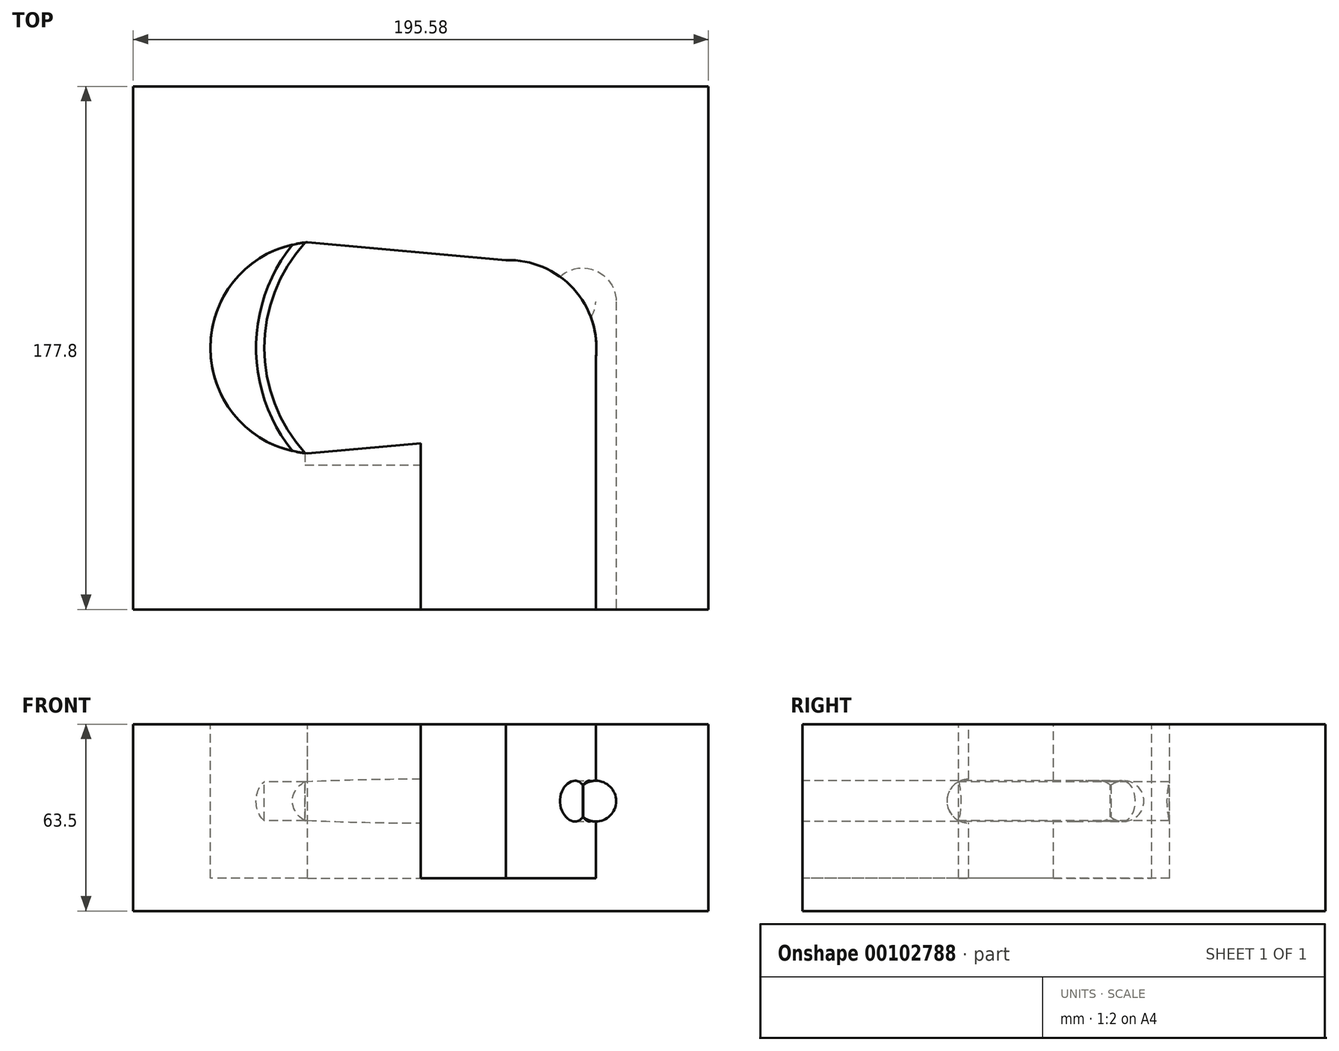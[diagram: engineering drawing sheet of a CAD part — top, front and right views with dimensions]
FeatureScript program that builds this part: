
annotation { "Feature Type Name" : "Feature", "Feature Type Description" : "" }
export const myFeature = defineFeature(function(context is Context, id is Id, definition is map)
    precondition{}
    {
        {
            var Q0;
            Q0=qCreatedBy(makeId("Top.planeOp"),FACE);
            var sketch = newSketch(context, id + "F0", { "sketchPlane" : qUnion([Q0])});
            skLineSegment(sketch, "E0.bottom", {"start": v(97.8, -88.9) * mm, "end": v(-97.8, -88.9) * mm});
            skLineSegment(sketch, "E0.top", {"start": v(97.8, 88.9) * mm, "end": v(-97.8, 88.9) * mm});
            skLineSegment(sketch, "E0.left", {"start": v(97.8, -88.9) * mm, "end": v(97.8, 88.9) * mm});
            skLineSegment(sketch, "E0.right", {"start": v(-97.8, -88.9) * mm, "end": v(-97.8, 88.9) * mm});
            skPoint(sketch, "E0.middle", {"position": v(0, 0) * mm});
            skSolve(sketch);
        }
        {
            var Q0;
            Q0 = qSketchRegion(id + "F0", true);
            extrude(context, id + "F1", {"entities" : qUnion([Q0]), "depth" : 63.5 * mm});
        }
        {
            var Q0;
            Q0=makeQuery(id+"F1.opExtrude","CAP_FACE",FACE,{"disambiguationData":[OSD([sQuery(id+"F0.wireOp",EDGE,"E0.bottom"),sQuery(id+"F0.wireOp",EDGE,"E0.top"),sQuery(id+"F0.wireOp",EDGE,"E0.left"),sQuery(id+"F0.wireOp",EDGE,"E0.right")])],"isStart":false});
            var sketch = newSketch(context, id + "F2", { "sketchPlane" : qUnion([Q0])});
            skLineSegment(sketch, "E1.bottom", {"start": v(94.69, -84.95) * mm, "end": v(59.47, -84.95) * mm});
            skLineSegment(sketch, "E1.top", {"start": v(94.69, 84.95) * mm, "end": v(-94.69, 84.95) * mm});
            skLineSegment(sketch, "E1.left", {"start": v(94.69, -84.95) * mm, "end": v(94.69, 84.95) * mm});
            skLineSegment(sketch, "E1.right", {"start": v(-94.69, -84.95) * mm, "end": v(-94.69, 84.95) * mm});
            skPoint(sketch, "E1.middle", {"position": v(0, 0) * mm});
            skArc(sketch, "E2", {"start": v(-26.3, 34.77) * mm, "mid": v(-71.59, 0) * mm, "end": v(-26.3, -34.77) * mm});
            skArc(sketch, "E3", {"start": v(59.47, 0) * mm, "mid": v(50.47, 21.25) * mm, "end": v(28.95, 29.57) * mm});
            skLineSegment(sketch, "E4", {"start": v(0, -32.4) * mm, "end": v(0, -92) * mm});
            skLineSegment(sketch, "E5", {"start": v(59.47, 0) * mm, "end": v(59.47, -92) * mm});
            skLineSegment(sketch, "E6", {"start": v(-38.52, 35.88) * mm, "end": v(28.95, 29.8) * mm});
            skPoint(sketch, "E6.endSnap0", {"position": v(28.95, 29.57) * mm});
            skArc(sketch, "E7", {"start": v(59.47, -3.6) * mm, "mid": v(51.89, 20.1) * mm, "end": v(28.95, 29.8) * mm});
            skLineSegment(sketch, "E8", {"start": v(-38.52, -35.88) * mm, "end": v(0, -32.4) * mm});
            skLineSegment(sketch, "E9", {"start": v(0, -92) * mm, "end": v(59.47, -92) * mm});
            skPoint(sketch, "E10.orphan", {"position": v(28.95, -29.8) * mm});
            skLineSegment(sketch, "E11.trimOffspring", {"start": v(0, -84.95) * mm, "end": v(-94.69, -84.95) * mm});
            skSolve(sketch);
        }
        {
            var Q0;
            {var subQ5=sQuery(id+"F2.wireOp",EDGE,"E7");Q0=makeQuery(id+"F2.imprint","IMPRINT",FACE,{"disambiguationData":[TD([[makeQuery(id+"F2.imprint","IMPRINT",EDGE,{"derivedFrom":subQ5}),1.0]])]});}
            extrude(context, id + "F3", {"entities" : qUnion([Q0]), "operationType" : NewBodyOperationType.REMOVE, "oppositeDirection" : true, "depth" : 52.32 * mm});
        }
        {
            var Q0;
            Q0=makeQuery(id+"F1.opExtrude","SWEPT_FACE",FACE,{"disambiguationData":[OSD([sQuery(id+"F0.wireOp",EDGE,"E0.bottom")])]});
            var sketch = newSketch(context, id + "F4", { "sketchPlane" : qUnion([Q0])});
            skCircle(sketch, "E12", {"center": v(59.47, 37.34) * mm, "radius": 6.92 * mm});
            skLineSegment(sketch, "E13", {"start": v(0, 75.98) * mm, "end": v(0, -24.75) * mm, "construction": true});
            skSolve(sketch);
        }
        {
            var Q0;
            {var subQ0=sQuery(id+"F4.wireOp",EDGE,"E12");var subQ1=makeQuery(id+"F3.boolean.opBoolean","COPY",EDGE,{"derivedFrom":makeQuery(id+"F3.opExtrude","SWEPT_EDGE",EDGE,{"disambiguationData":[OSD([sQuery(id+"F0.wireOp",EDGE,"E0.bottom"),sQuery(id+"F2.wireOp",EDGE,"E5")])]})});var subQ2=makeQuery(id+"F4.imprint","INTERSECT",VERTEX,{"disambiguationData":[OD(0.0)],"derivedFrom":[subQ1,subQ0]});Q0=makeQuery(id+"F4.imprint","IMPRINT",FACE,{"disambiguationData":[TD([[makeQuery(id+"F4.imprint","IMPRINT",EDGE,{"disambiguationData":[TD([[subQ2,-1.0]])],"derivedFrom":subQ0}),1.0]])]});}
            var Q1;
            {var subQ0=sQuery(id+"F4.wireOp",EDGE,"E12");var subQ1=makeQuery(id+"F3.boolean.opBoolean","COPY",EDGE,{"derivedFrom":makeQuery(id+"F3.opExtrude","SWEPT_EDGE",EDGE,{"disambiguationData":[OSD([sQuery(id+"F0.wireOp",EDGE,"E0.bottom"),sQuery(id+"F2.wireOp",EDGE,"E5")])]})});var subQ2=makeQuery(id+"F4.imprint","INTERSECT",VERTEX,{"disambiguationData":[OD(0.0)],"derivedFrom":[subQ1,subQ0]});Q1=makeQuery(id+"F4.imprint","IMPRINT",FACE,{"disambiguationData":[TD([[makeQuery(id+"F4.imprint","IMPRINT",EDGE,{"disambiguationData":[TD([[subQ2,1.0]])],"derivedFrom":subQ0}),1.0]])]});}
            var Q2;
            Q2=sQuery(id+"F4.wireOp",EDGE,"E12");
            extrude(context, id + "F5", {"entities" : qUnion([Q0, Q1]), "operationType" : NewBodyOperationType.REMOVE, "surfaceEntities" : qUnion([Q2]), "oppositeDirection" : true, "depth" : 104.65 * mm});
        }
        {
            var Q0;
            Q0=makeQuery(id+"F5.boolean.opBoolean","COPY",FACE,{"derivedFrom":makeQuery(id+"F5.opExtrude","CAP_FACE",FACE,{"disambiguationData":[OSD([sQuery(id+"F4.wireOp",EDGE,"E12")])],"isStart":false})});
            var sketch = newSketch(context, id + "F6", { "sketchPlane" : qUnion([Q0])});
            skCircle(sketch, "E14", {"center": v(59.47, 37.34) * mm, "radius": 7.04 * mm});
            skLineSegment(sketch, "E15", {"start": v(54.97, 65.9) * mm, "end": v(54.97, -27.92) * mm, "construction": true});
            skSolve(sketch);
        }
        {
            var Q0;
            {var subQ0=sQuery(id+"F4.wireOp",EDGE,"E12");Q0=makeQuery(id+"F6.imprint","IMPRINT",FACE,{"disambiguationData":[TD([[makeQuery(id+"F6.imprint","IMPRINT",EDGE,{"derivedFrom":makeQuery(id+"F5.boolean.opBoolean","COPY",EDGE,{"derivedFrom":makeQuery(id+"F5.opExtrude","CAP_EDGE",EDGE,{"disambiguationData":[OSD([subQ0])],"isStart":false})})}),1.0]])]});}
            var Q1;
            Q1=sQuery(id+"F6.wireOp",EDGE,"E15");
            revolve(context, id + "F7", {"operationType" : NewBodyOperationType.REMOVE, "entities" : qUnion([Q0]), "axis" : qUnion([Q1]), "revolveType" : RevolveType.FULL, "oppositeDirection" : true});
        }
        {
            var Q0;
            Q0=makeQuery(id+"F3.boolean.opBoolean","COPY",FACE,{"derivedFrom":makeQuery(id+"F3.opExtrude","SWEPT_FACE",FACE,{"disambiguationData":[OSD([sQuery(id+"F2.wireOp",EDGE,"E4")])]})});
            var sketch = newSketch(context, id + "F8", { "sketchPlane" : qUnion([Q0])});
            skCircle(sketch, "E16", {"center": v(-32.4, 37.34) * mm, "radius": 7.42 * mm});
            skLineSegment(sketch, "E17", {"start": v(0.63, -14.17) * mm, "end": v(0.63, 89.5) * mm, "construction": true});
            skSolve(sketch);
        }
        {
            var Q0;
            Q0 = qSketchRegion(id + "F8", true);
            extrude(context, id + "F9", {"entities" : qUnion([Q0]), "operationType" : NewBodyOperationType.REMOVE, "oppositeDirection" : true, "depth" : 39.37 * mm});
        }
        {
            var Q0;
            Q0=qCreatedBy(makeId("Right.planeOp"),FACE);
            var sketch = newSketch(context, id + "F10", { "sketchPlane" : qUnion([Q0])});
            skLineSegment(sketch, "E18", {"start": v(0, 0) * mm, "end": v(0, 78.57) * mm, "construction": true});
            skSolve(sketch);
        }
        {
            var Q0;
            Q0=makeQuery(id+"F9.boolean.opBoolean","COPY",FACE,{"derivedFrom":makeQuery(id+"F9.opExtrude","CAP_FACE",FACE,{"disambiguationData":[OSD([sQuery(id+"F8.wireOp",EDGE,"E16")])],"isStart":false})});
            var Q1;
            Q1=sQuery(id+"F10.wireOp",EDGE,"E18");
            revolve(context, id + "F11", {"operationType" : NewBodyOperationType.ADD, "entities" : qUnion([Q0]), "axis" : qUnion([Q1]), "revolveType" : RevolveType.ONE_DIRECTION, "oppositeDirection" : true, "angle" : 150 * degree});
        }
    });
